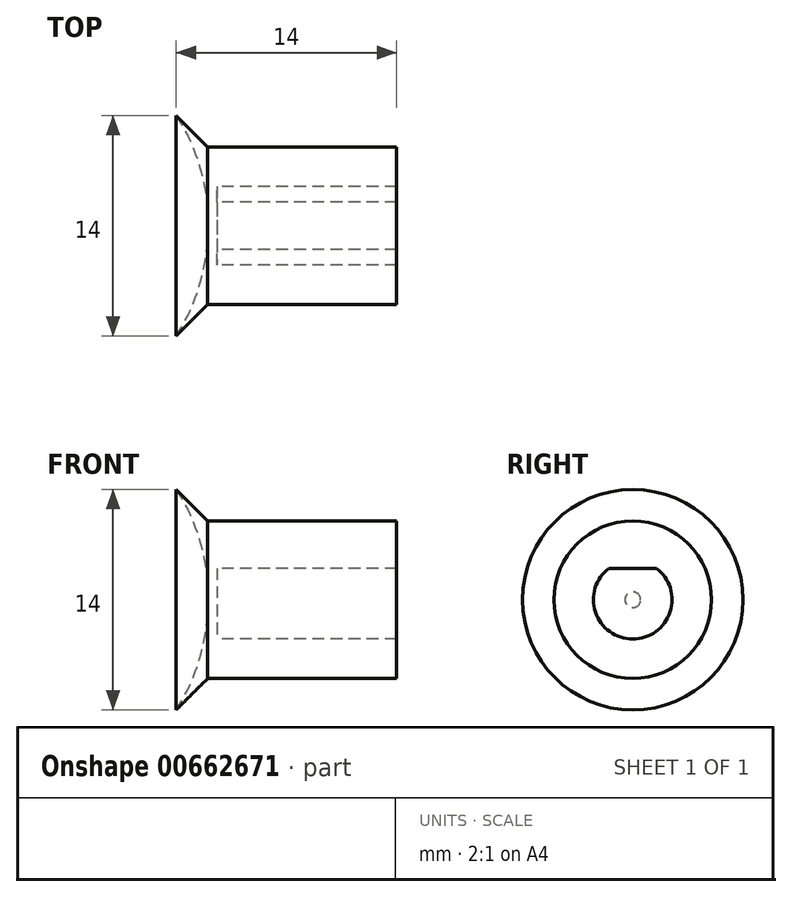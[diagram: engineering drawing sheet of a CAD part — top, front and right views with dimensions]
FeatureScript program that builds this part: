
annotation { "Feature Type Name" : "Feature", "Feature Type Description" : "" }
export const myFeature = defineFeature(function(context is Context, id is Id, definition is map)
    precondition{}
    {
        {
            var Q0;
            Q0=qCreatedBy(makeId("Right.planeOp"),FACE);
            var sketch = newSketch(context, id + "F0", { "sketchPlane" : qUnion([Q0])});
            skArc(sketch, "E0", {"start": v(-1.5, 2) * mm, "mid": v(0, -2.5) * mm, "end": v(1.5, 2) * mm});
            skCircle(sketch, "E1", {"center": v(0, 0) * mm, "radius": 5 * mm});
            skLineSegment(sketch, "E2", {"start": v(-1.5, 2) * mm, "end": v(1.5, 2) * mm});
            skSolve(sketch);
        }
        {
            var Q0;
            Q0=makeQuery(id+"F0.imprint","IMPRINT",FACE,{"disambiguationData":[TD([[makeQuery(id+"F0.imprint","IMPRINT",EDGE,{"derivedFrom":sQuery(id+"F0.wireOp",EDGE,"E0")}),-1.0]])]});
            extrude(context, id + "F1", {"entities" : qUnion([Q0]), "depth" : 12 * mm});
        }
        {
            var Q0;
            Q0=qCreatedBy(makeId("Top.planeOp"),FACE);
            var sketch = newSketch(context, id + "F2", { "sketchPlane" : qUnion([Q0])});
            skLineSegment(sketch, "E3", {"start": v(0, 5) * mm, "end": v(-2, 7) * mm});
            skArc(sketch, "E4", {"start": v(-2, 7) * mm, "mid": v(-0.47, 3.65) * mm, "end": v(0, 0) * mm});
            skLineSegment(sketch, "E5.0", {"start": v(0, 5) * mm, "end": v(0, -5) * mm});
            skLineSegment(sketch, "E6", {"start": v(0, 0) * mm, "end": v(-7.04, 0) * mm});
            skSolve(sketch);
        }
        {
            var Q0;
            Q0=makeQuery(id+"F1.opExtrude","CAP_FACE",FACE,{"disambiguationData":[OSD([sQuery(id+"F0.wireOp",EDGE,"E0"),sQuery(id+"F0.wireOp",EDGE,"E1"),sQuery(id+"F0.wireOp",EDGE,"E2")])],"isStart":true});
            var sketch = newSketch(context, id + "F3", { "sketchPlane" : qUnion([Q0])});
            skCircle(sketch, "E7.0", {"center": v(0, 0) * mm, "radius": 5 * mm});
            skSolve(sketch);
        }
        {
            var Q0;
            Q0=qSketchRegion(id+"F3",true);
            extrude(context, id + "F4", {"entities" : qUnion([Q0]), "operationType" : NewBodyOperationType.ADD, "oppositeDirection" : true, "depth" : .6 * mm});
        }
        {
            var Q0;
            {var subQ0=sQuery(id+"F2.wireOp",EDGE,"E3");Q0=makeQuery(id+"F2.imprint","IMPRINT",FACE,{"disambiguationData":[TD([[makeQuery(id+"F2.imprint","IMPRINT",EDGE,{"derivedFrom":subQ0}),1.0]])]});}
            var Q1;
            Q1=sQuery(id+"F2.wireOp",EDGE,"E6");
            revolve(context, id + "F5", {"operationType" : NewBodyOperationType.ADD, "entities" : qUnion([Q0]), "axis" : qUnion([Q1]), "revolveType" : RevolveType.FULL});
        }
    });
